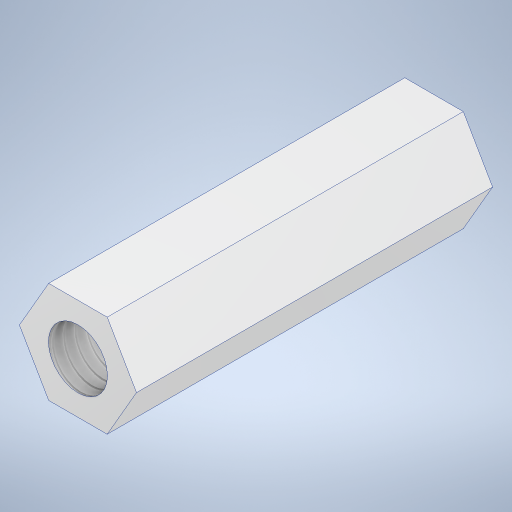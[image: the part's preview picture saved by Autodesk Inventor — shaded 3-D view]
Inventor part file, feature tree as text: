
AUTODESK INVENTOR PART (.ipt)
format: ipt  version: 2024 (Build 280153000, 153)  size: 223,232 bytes
history: native  units: in
note: dims shown in document units (in); Inventor stores cm internally (conversion verified against a paired STEP export)
features: extrude x1, thread x1, sketch x1
ambient origin geometry x8: Origin, YZ Plane, XZ Plane, XY Plane, X Axis, Y Axis, Z Axis, Center Point
bodies: Solid1 (feature_tree)
feature tree (3):
  extrude  "Extrusion1"  Depth=1.756in
  thread  "Thread1"  [1 undecoded]
  sketch  "Sketch1"  dims[d0=0.5in d1=0.291in d2=1.756in d3=0.0in d4=1.756in d5=0.0in]
note: 1 required parameter value undecoded (feature->parameter linkage not recoverable at this tier; creation-order binding heuristic only, values carry confidence <= 0.55)
